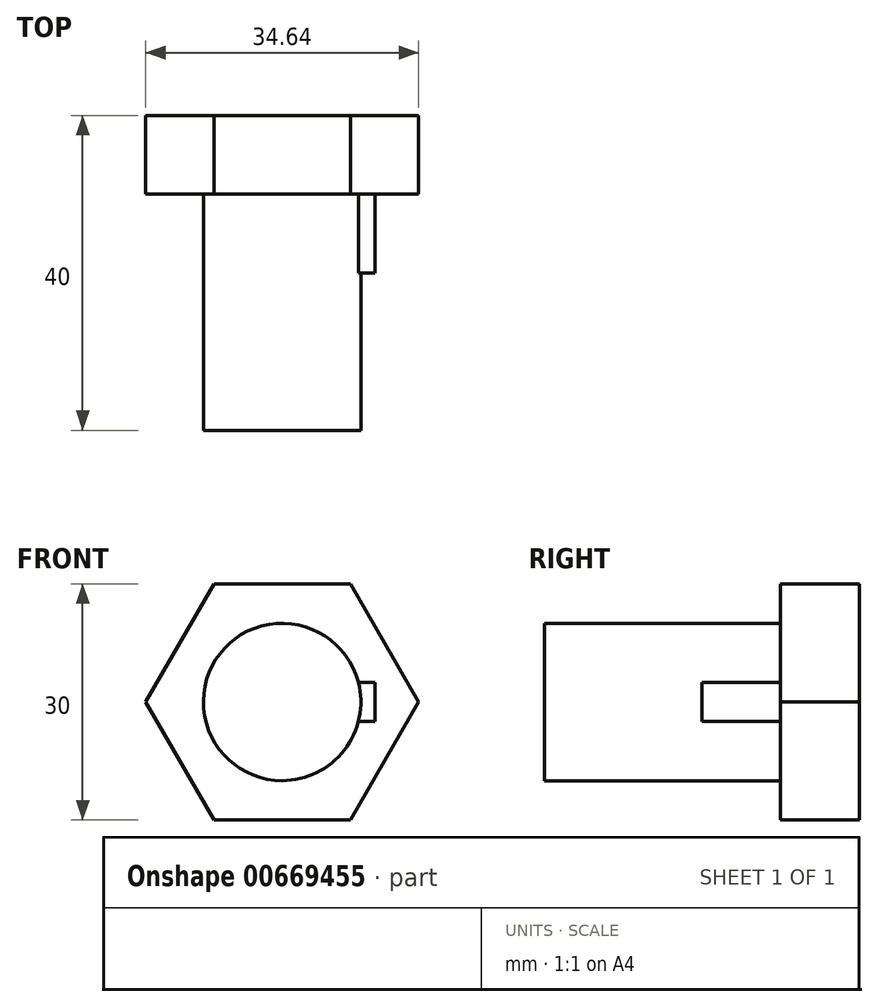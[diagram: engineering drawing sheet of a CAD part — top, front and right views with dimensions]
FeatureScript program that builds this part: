
annotation { "Feature Type Name" : "Feature", "Feature Type Description" : "" }
export const myFeature = defineFeature(function(context is Context, id is Id, definition is map)
    precondition{}
    {
        {
            var Q0;
            Q0=qCreatedBy(makeId("Front.planeOp"),FACE);
            var sketch = newSketch(context, id + "F0", { "sketchPlane" : qUnion([Q0])});
            skCircle(sketch, "E0.cCircle", {"center": v(0, 0) * mm, "radius": 15 * mm, "construction": true});
            skLineSegment(sketch, "E0.0", {"start": v(-8.66, 15) * mm, "end": v(8.66, 15) * mm});
            skLineSegment(sketch, "E0.1", {"start": v(8.66, 15) * mm, "end": v(17.32, 0) * mm});
            skLineSegment(sketch, "E0.2", {"start": v(17.32, 0) * mm, "end": v(8.66, -15) * mm});
            skLineSegment(sketch, "E0.3", {"start": v(8.66, -15) * mm, "end": v(-8.66, -15) * mm});
            skLineSegment(sketch, "E0.4", {"start": v(-8.66, -15) * mm, "end": v(-17.32, 0) * mm});
            skLineSegment(sketch, "E0.5", {"start": v(-17.32, 0) * mm, "end": v(-8.66, 15) * mm});
            skPoint(sketch, "E0.0.midPoint", {"position": v(0, 15) * mm});
            skCircle(sketch, "E1", {"center": v(0, 0) * mm, "radius": 10 * mm});
            skLineSegment(sketch, "E2", {"start": v(11.8, 0) * mm, "end": v(11.8, 2.5) * mm});
            skLineSegment(sketch, "E3", {"start": v(11.8, 0) * mm, "end": v(11.8, -2.5) * mm});
            skLineSegment(sketch, "E4", {"start": v(11.8, -2.5) * mm, "end": v(9.68, -2.5) * mm});
            skLineSegment(sketch, "E5", {"start": v(11.8, 2.5) * mm, "end": v(9.68, 2.5) * mm});
            skSolve(sketch);
        }
        {
            var Q0;
            Q0=makeQuery(id+"F0.imprint","IMPRINT",FACE,{"disambiguationData":[TD([[makeQuery(id+"F0.imprint","IMPRINT",EDGE,{"derivedFrom":sQuery(id+"F0.wireOp",EDGE,"E0.0")}),-1.0]])]});
            extrude(context, id + "F1", {"entities" : qUnion([Q0]), "depth" : 10 * mm, "offsetDistance" : 25 * mm});
        }
        {
            var Q0;
            {var subQ0=sQuery(id+"F0.wireOp",EDGE,"E1");var subQ1=makeQuery(id+"F0.imprint","INTERSECT",VERTEX,{"derivedFrom":[subQ0,sQuery(id+"F0.wireOp",EDGE,"E4")]});Q0=makeQuery(id+"F0.imprint","IMPRINT",FACE,{"disambiguationData":[TD([[makeQuery(id+"F0.imprint","IMPRINT",EDGE,{"disambiguationData":[TD([[subQ1,1.0]])],"derivedFrom":subQ0}),1.0]])]});}
            extrude(context, id + "F2", {"entities" : qUnion([Q0]), "operationType" : NewBodyOperationType.ADD, "depth" : 40 * mm, "offsetDistance" : 25 * mm});
        }
        {
            var Q0;
            Q0=makeQuery(id+"F0.imprint","IMPRINT",FACE,{"disambiguationData":[TD([[makeQuery(id+"F0.imprint","IMPRINT",EDGE,{"derivedFrom":sQuery(id+"F0.wireOp",EDGE,"E2")}),1.0]])]});
            extrude(context, id + "F3", {"entities" : qUnion([Q0]), "operationType" : NewBodyOperationType.ADD, "depth" : 20 * mm, "offsetDistance" : 25 * mm});
        }
    });
